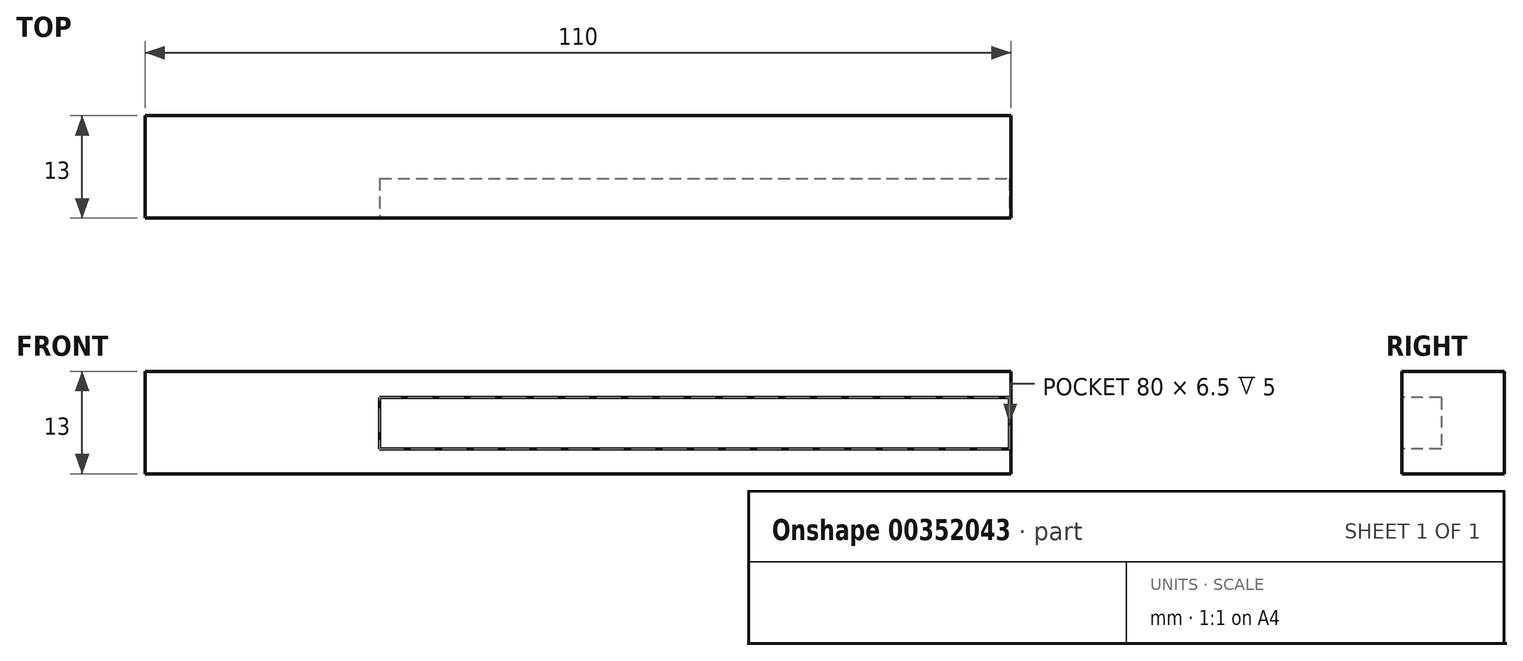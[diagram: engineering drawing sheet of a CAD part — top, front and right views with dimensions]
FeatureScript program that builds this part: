
annotation { "Feature Type Name" : "Feature", "Feature Type Description" : "" }
export const myFeature = defineFeature(function(context is Context, id is Id, definition is map)
    precondition{}
    {
        {
            var Q0;
            Q0=qCreatedBy(makeId("Right.planeOp"),FACE);
            var sketch = newSketch(context, id + "F0", { "sketchPlane" : qUnion([Q0])});
            skLineSegment(sketch, "E0.bottom", {"start": v(-6.5, 6.5) * mm, "end": v(6.5, 6.5) * mm});
            skLineSegment(sketch, "E0.top", {"start": v(-6.5, -6.5) * mm, "end": v(6.5, -6.5) * mm});
            skLineSegment(sketch, "E0.left", {"start": v(-6.5, 6.5) * mm, "end": v(-6.5, -6.5) * mm});
            skLineSegment(sketch, "E0.right", {"start": v(6.5, 6.5) * mm, "end": v(6.5, -6.5) * mm});
            skSolve(sketch);
        }
        {
            var Q0;
            Q0=qSketchRegion(id+"F0",true);
            extrude(context, id + "F1", {"entities" : qUnion([Q0]), "depth" : 110 * mm});
        }
        {
            var Q0;
            Q0=makeQuery(id+"F1.opExtrude","SWEPT_FACE",FACE,{"disambiguationData":[OSD([sQuery(id+"F0.wireOp",EDGE,"E0.left")])]});
            var sketch = newSketch(context, id + "F2", { "sketchPlane" : qUnion([Q0])});
            skLineSegment(sketch, "E1.bottom", {"start": v(29.81, 3.18) * mm, "end": v(109.81, 3.18) * mm});
            skLineSegment(sketch, "E1.top", {"start": v(29.81, -3.32) * mm, "end": v(109.81, -3.32) * mm});
            skLineSegment(sketch, "E1.left", {"start": v(29.81, 3.18) * mm, "end": v(29.81, -3.32) * mm});
            skLineSegment(sketch, "E1.right", {"start": v(109.81, 3.18) * mm, "end": v(109.81, -3.32) * mm});
            skSolve(sketch);
        }
        {
            var Q0;
            Q0=makeQuery(id+"F2.imprint","IMPRINT",FACE,{"disambiguationData":[TD([[makeQuery(id+"F2.imprint","IMPRINT",EDGE,{"derivedFrom":sQuery(id+"F2.wireOp",EDGE,"E1.bottom")}),-1.0]])]});
            extrude(context, id + "F3", {"entities" : qUnion([Q0]), "operationType" : NewBodyOperationType.REMOVE, "oppositeDirection" : true, "depth" : 5 * mm});
        }
    });
